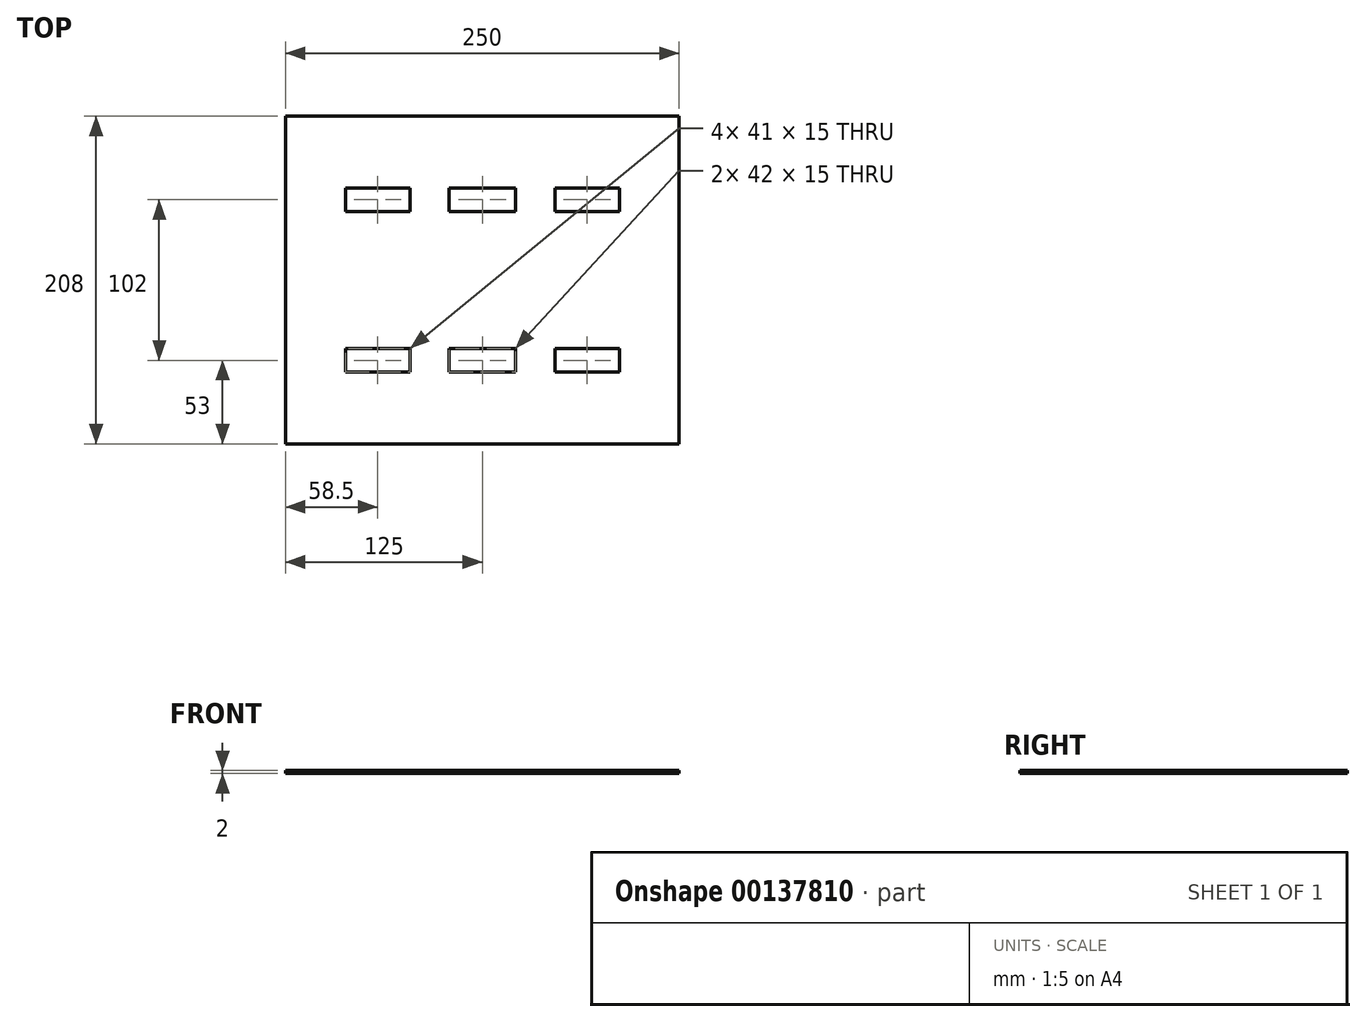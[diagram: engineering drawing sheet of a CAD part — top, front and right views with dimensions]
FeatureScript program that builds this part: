
annotation { "Feature Type Name" : "Feature", "Feature Type Description" : "" }
export const myFeature = defineFeature(function(context is Context, id is Id, definition is map)
    precondition{}
    {
        {
            var Q0;
            Q0=qCreatedBy(makeId("Top.planeOp"),FACE);
            var sketch = newSketch(context, id + "F0", { "sketchPlane" : qUnion([Q0])});
            skLineSegment(sketch, "E0.bottom", {"start": v(125, -104) * mm, "end": v(-125, -104) * mm});
            skLineSegment(sketch, "E0.top", {"start": v(125, 104) * mm, "end": v(-125, 104) * mm});
            skLineSegment(sketch, "E0.left", {"start": v(125, -104) * mm, "end": v(125, 104) * mm});
            skLineSegment(sketch, "E0.right", {"start": v(-125, -104) * mm, "end": v(-125, 104) * mm});
            skPoint(sketch, "E0.middle", {"position": v(0, 0) * mm});
            skSolve(sketch);
        }
        {
            var Q0;
            Q0 = qSketchRegion(id + "F0", true);
            extrude(context, id + "F1", {"entities" : qUnion([Q0]), "depth" : 2 * mm});
        }
        {
            var Q0;
            Q0=makeQuery(id+"F1.opExtrude","CAP_FACE",FACE,{"disambiguationData":[OSD([sQuery(id+"F0.wireOp",EDGE,"E0.bottom"),sQuery(id+"F0.wireOp",EDGE,"E0.top"),sQuery(id+"F0.wireOp",EDGE,"E0.left"),sQuery(id+"F0.wireOp",EDGE,"E0.right")])],"isStart":false});
            var sketch = newSketch(context, id + "F2", { "sketchPlane" : qUnion([Q0])});
            skLineSegment(sketch, "E1.bottom", {"start": v(104.5, -81) * mm, "end": v(-104.5, -81) * mm, "construction": true});
            skLineSegment(sketch, "E1.top", {"start": v(104.5, 81) * mm, "end": v(-104.5, 81) * mm, "construction": true});
            skLineSegment(sketch, "E1.left", {"start": v(104.5, -81) * mm, "end": v(104.5, 81) * mm, "construction": true});
            skLineSegment(sketch, "E1.right", {"start": v(-104.5, -81) * mm, "end": v(-104.5, 81) * mm, "construction": true});
            skPoint(sketch, "E1.middle", {"position": v(0, 0) * mm});
            skLineSegment(sketch, "E2.bottom", {"start": v(21, 43.5) * mm, "end": v(-21, 43.5) * mm});
            skLineSegment(sketch, "E2.top", {"start": v(21, 58.5) * mm, "end": v(-21, 58.5) * mm});
            skLineSegment(sketch, "E2.left", {"start": v(21, 43.5) * mm, "end": v(21, 58.5) * mm});
            skLineSegment(sketch, "E2.right", {"start": v(-21, 43.5) * mm, "end": v(-21, 58.5) * mm});
            skPoint(sketch, "E2.middle", {"position": v(0, 51) * mm});
            skLineSegment(sketch, "E3.bottom", {"start": v(87, 43.5) * mm, "end": v(46, 43.5) * mm});
            skLineSegment(sketch, "E3.top", {"start": v(87, 58.5) * mm, "end": v(46, 58.5) * mm});
            skLineSegment(sketch, "E3.left", {"start": v(87, 43.5) * mm, "end": v(87, 58.5) * mm});
            skLineSegment(sketch, "E3.right", {"start": v(46, 43.5) * mm, "end": v(46, 58.5) * mm});
            skPoint(sketch, "E3.middle", {"position": v(66.5, 51) * mm});
            skPoint(sketch, "E3.middle.positionSnap0", {"position": v(21, 51) * mm});
            skPoint(sketch, "E3.centerSnap0", {"position": v(21, 51) * mm});
            skLineSegment(sketch, "E4.bottom", {"start": v(-46, 43.5) * mm, "end": v(-87, 43.5) * mm});
            skLineSegment(sketch, "E4.top", {"start": v(-46, 58.5) * mm, "end": v(-87, 58.5) * mm});
            skLineSegment(sketch, "E4.left", {"start": v(-46, 43.5) * mm, "end": v(-46, 58.5) * mm});
            skLineSegment(sketch, "E4.right", {"start": v(-87, 43.5) * mm, "end": v(-87, 58.5) * mm});
            skPoint(sketch, "E4.middle", {"position": v(-66.5, 51) * mm});
            skLineSegment(sketch, "E5.bottom", {"start": v(21, -58.5) * mm, "end": v(-21, -58.5) * mm});
            skLineSegment(sketch, "E5.top", {"start": v(21, -43.5) * mm, "end": v(-21, -43.5) * mm});
            skLineSegment(sketch, "E5.left", {"start": v(21, -58.5) * mm, "end": v(21, -43.5) * mm});
            skLineSegment(sketch, "E5.right", {"start": v(-21, -58.5) * mm, "end": v(-21, -43.5) * mm});
            skPoint(sketch, "E5.middle", {"position": v(0, -51) * mm});
            skPoint(sketch, "E5.middle.positionSnap0", {"position": v(0, 43.5) * mm});
            skPoint(sketch, "E5.centerSnap0", {"position": v(0, 43.5) * mm});
            skLineSegment(sketch, "E6.bottom", {"start": v(87, -58.5) * mm, "end": v(46, -58.5) * mm});
            skLineSegment(sketch, "E6.top", {"start": v(87, -43.5) * mm, "end": v(46, -43.5) * mm});
            skLineSegment(sketch, "E6.left", {"start": v(87, -58.5) * mm, "end": v(87, -43.5) * mm});
            skLineSegment(sketch, "E6.right", {"start": v(46, -58.5) * mm, "end": v(46, -43.5) * mm});
            skPoint(sketch, "E6.middle", {"position": v(66.5, -51) * mm});
            skLineSegment(sketch, "E7.bottom", {"start": v(-46, -58.5) * mm, "end": v(-87, -58.5) * mm});
            skLineSegment(sketch, "E7.top", {"start": v(-46, -43.5) * mm, "end": v(-87, -43.5) * mm});
            skLineSegment(sketch, "E7.left", {"start": v(-46, -58.5) * mm, "end": v(-46, -43.5) * mm});
            skLineSegment(sketch, "E7.right", {"start": v(-87, -58.5) * mm, "end": v(-87, -43.5) * mm});
            skPoint(sketch, "E7.middle", {"position": v(-66.5, -51) * mm});
            skPoint(sketch, "E7.middle.positionSnap0", {"position": v(-66.5, 43.5) * mm});
            skPoint(sketch, "E7.cornerSnap0", {"position": v(0, -58.5) * mm});
            skPoint(sketch, "E7.centerSnap0", {"position": v(-66.5, 43.5) * mm});
            skSolve(sketch);
        }
        {
            var Q0;
            Q0 = qSketchRegion(id + "F2", true);
            extrude(context, id + "F3", {"entities" : qUnion([Q0]), "operationType" : NewBodyOperationType.REMOVE, "endBound" : BoundingType.THROUGH_ALL, "oppositeDirection" : true, "depth" : 25 * mm});
        }
    });
